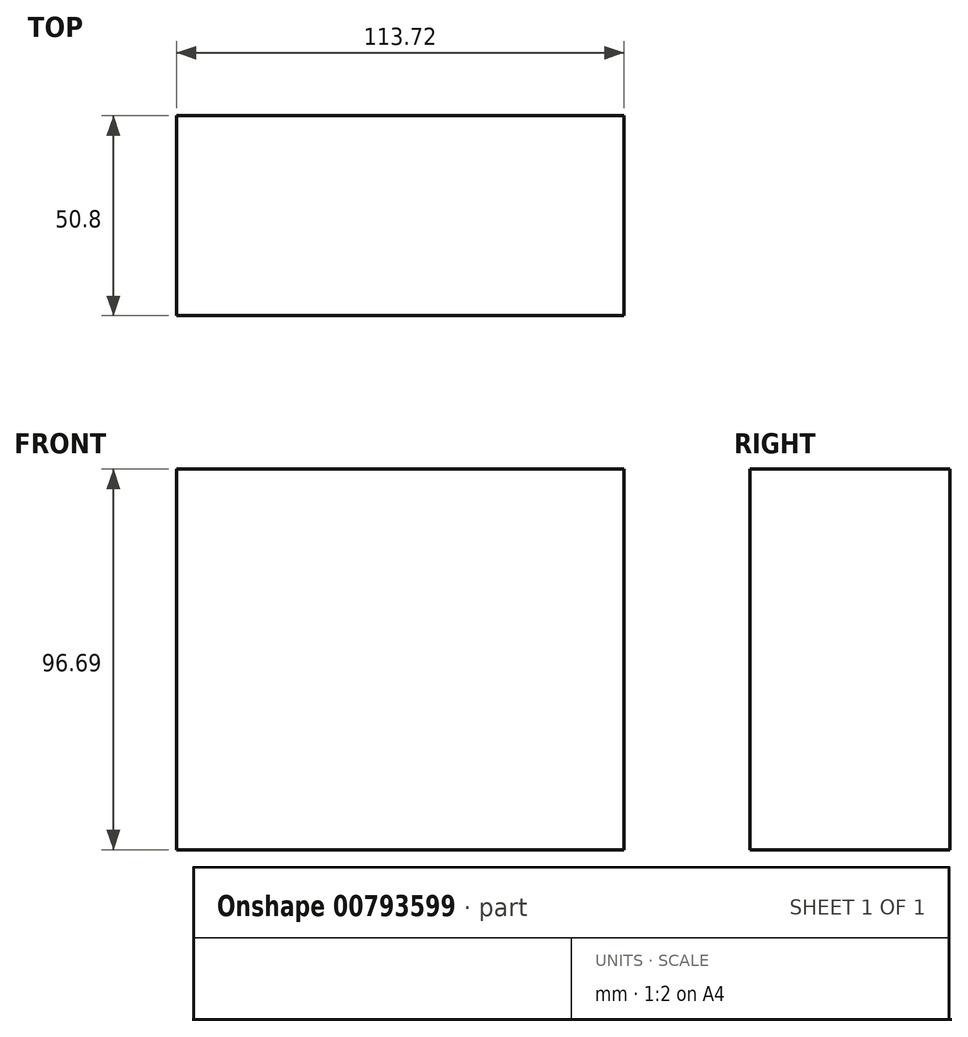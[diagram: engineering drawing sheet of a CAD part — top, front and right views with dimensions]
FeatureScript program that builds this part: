
annotation { "Feature Type Name" : "Feature", "Feature Type Description" : "" }
export const myFeature = defineFeature(function(context is Context, id is Id, definition is map)
    precondition{}
    {
        {
            var Q0;
            Q0=qCreatedBy(makeId("Front.planeOp"),FACE);
            var sketch = newSketch(context, id + "F0", { "sketchPlane" : qUnion([Q0])});
            skLineSegment(sketch, "E0.bottom", {"start": v(-56.65, 43.82) * mm, "end": v(57.07, 43.82) * mm});
            skLineSegment(sketch, "E0.top", {"start": v(-56.65, -52.87) * mm, "end": v(57.07, -52.87) * mm});
            skLineSegment(sketch, "E0.left", {"start": v(-56.65, 43.82) * mm, "end": v(-56.65, -52.87) * mm});
            skLineSegment(sketch, "E0.right", {"start": v(57.07, 43.82) * mm, "end": v(57.07, -52.87) * mm});
            skSolve(sketch);
        }
        {
            var Q0;
            Q0=makeQuery(id+"F0.imprint","IMPRINT",FACE,{"disambiguationData":[TD([[makeQuery(id+"F0.imprint","IMPRINT",EDGE,{"derivedFrom":sQuery(id+"F0.wireOp",EDGE,"E0.bottom")}),-1.0]])]});
            extrude(context, id + "F1", {"entities" : qUnion([Q0]), "depth" : 50.8 * mm, "offsetDistance" : 25.4 * mm});
        }
    });
